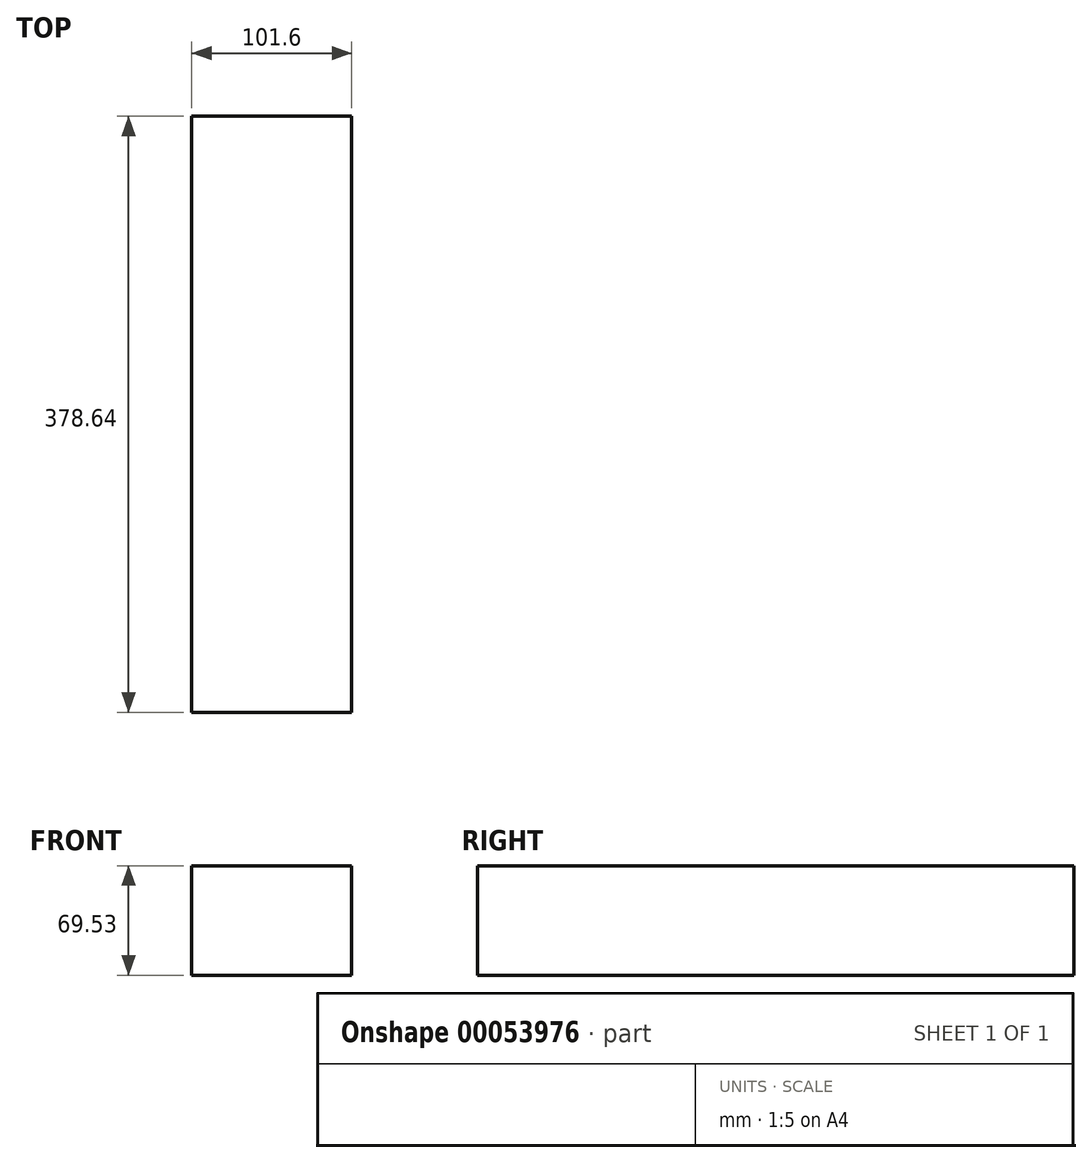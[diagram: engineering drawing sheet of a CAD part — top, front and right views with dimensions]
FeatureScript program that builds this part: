
annotation { "Feature Type Name" : "Feature", "Feature Type Description" : "" }
export const myFeature = defineFeature(function(context is Context, id is Id, definition is map)
    precondition{}
    {
        {
            var Q0;
            Q0=qCreatedBy(makeId("Right.planeOp"),FACE);
            var sketch = newSketch(context, id + "F0", { "sketchPlane" : qUnion([Q0])});
            skLineSegment(sketch, "E0.rect.bottom", {"start": v(-189.32, -37.42) * mm, "end": v(189.32, -37.42) * mm});
            skLineSegment(sketch, "E0.rect.top", {"start": v(-189.32, 32.11) * mm, "end": v(189.32, 32.11) * mm});
            skLineSegment(sketch, "E0.rect.left", {"start": v(-189.32, -37.42) * mm, "end": v(-189.32, 32.11) * mm});
            skLineSegment(sketch, "E0.rect.right", {"start": v(189.32, -37.42) * mm, "end": v(189.32, 32.11) * mm});
            skPoint(sketch, "E0.rect.middle", {"position": v(0, -2.66) * mm});
            skSolve(sketch);
        }
        {
            var Q0;
            Q0=makeQuery(id+"F0.imprint","IMPRINT",FACE,{"disambiguationData":[TD([[makeQuery(id+"F0.imprint","IMPRINT",EDGE,{"derivedFrom":sQuery(id+"F0.wireOp",EDGE,"E0.rect.bottom")}),1.0]])]});
            extrude(context, id + "F1", {"entities" : qUnion([Q0]), "depth" : 101.6 * mm});
        }
    });
